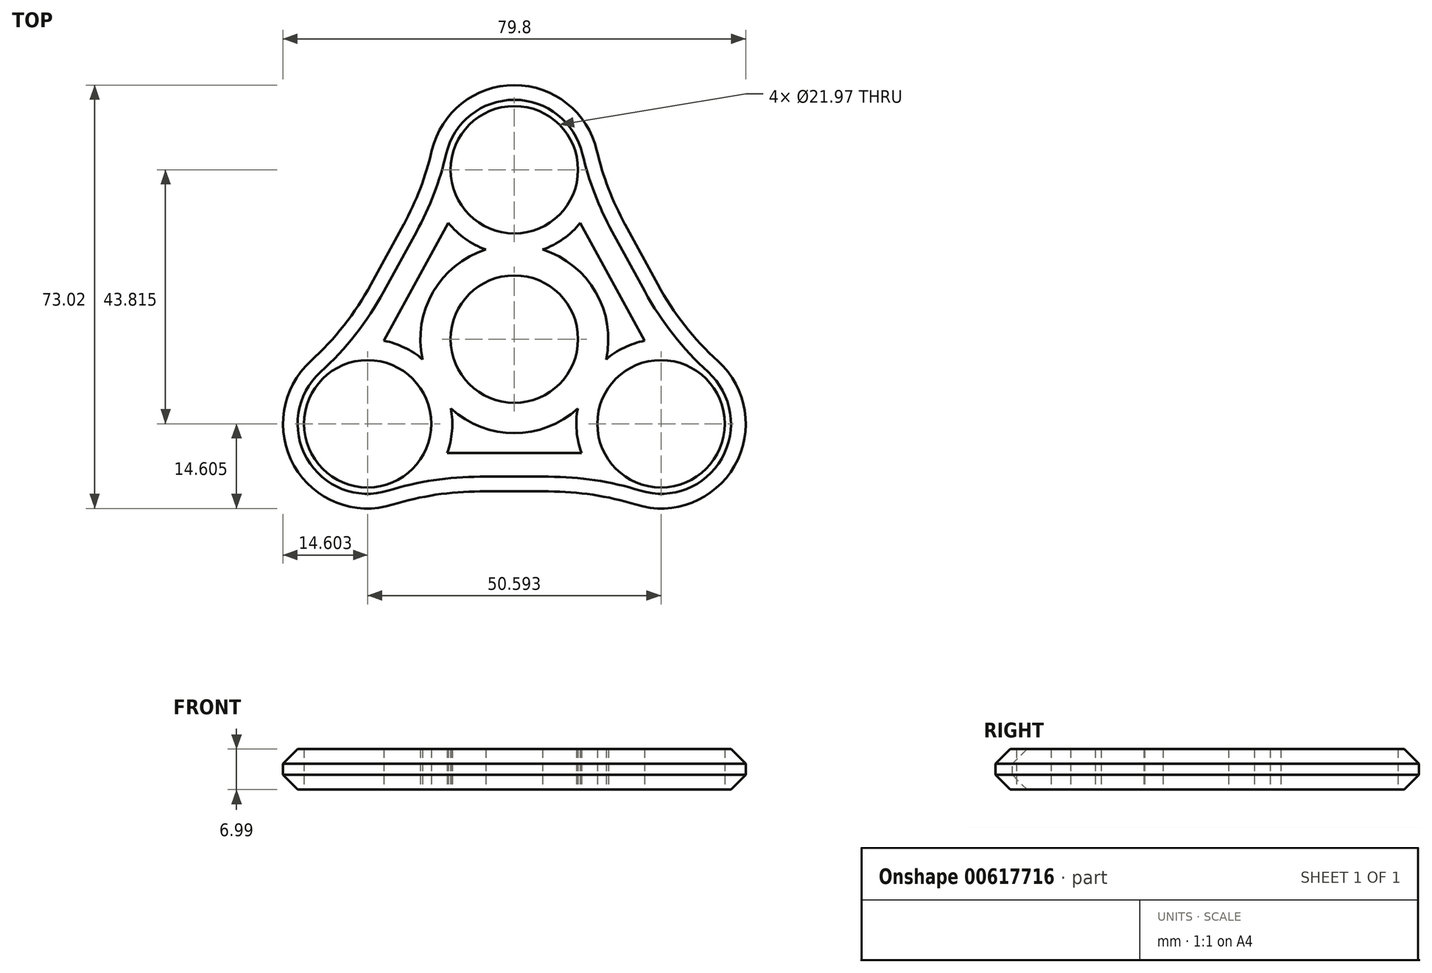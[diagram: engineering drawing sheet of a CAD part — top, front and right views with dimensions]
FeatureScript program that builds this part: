
annotation { "Feature Type Name" : "Feature", "Feature Type Description" : "" }
export const myFeature = defineFeature(function(context is Context, id is Id, definition is map)
    precondition{}
    {
        {
            var Q0;
            Q0=qCreatedBy(makeId("Top.planeOp"),FACE);
            var sketch = newSketch(context, id + "F0", { "sketchPlane" : qUnion([Q0])});
            skCircle(sketch, "E0", {"center": v(0, 0) * mm, "radius": 10.99 * mm});
            skLineSegment(sketch, "E1", {"start": v(0, 0) * mm, "end": v(0, 29.21) * mm});
            skLineSegment(sketch, "E2", {"start": v(0, 0) * mm, "end": v(25.3, -14.6) * mm});
            skLineSegment(sketch, "E3", {"start": v(0, 0) * mm, "end": v(-25.3, -14.6) * mm});
            skCircle(sketch, "E4", {"center": v(-25.3, -14.6) * mm, "radius": 10.99 * mm});
            skCircle(sketch, "E5", {"center": v(25.3, -14.6) * mm, "radius": 10.99 * mm});
            skCircle(sketch, "E6", {"center": v(0, 29.21) * mm, "radius": 10.99 * mm});
            skCircle(sketch, "E7", {"center": v(-25.3, -14.6) * mm, "radius": 14.6 * mm});
            skCircle(sketch, "E8", {"center": v(0, 29.21) * mm, "radius": 14.6 * mm});
            skCircle(sketch, "E9", {"center": v(25.3, -14.6) * mm, "radius": 14.6 * mm});
            skLineSegment(sketch, "E10", {"start": v(-16.5, -26.27) * mm, "end": v(16.51, -26.27) * mm});
            skLineSegment(sketch, "E11", {"start": v(11.38, 20.05) * mm, "end": v(22.47, -0.28) * mm});
            skLineSegment(sketch, "E12", {"start": v(-11.58, -19.62) * mm, "end": v(11.58, -19.62) * mm});
            skLineSegment(sketch, "E13", {"start": v(14.56, 28.07) * mm, "end": v(30.38, -0.91) * mm});
            skLineSegment(sketch, "E14", {"start": v(-14.56, 28.07) * mm, "end": v(-30.38, -0.91) * mm});
            skLineSegment(sketch, "E15", {"start": v(-11.38, 20.05) * mm, "end": v(-22.47, -0.28) * mm});
            skPoint(sketch, "E15.endSnap0", {"position": v(-22.47, 13.58) * mm});
            skCircle(sketch, "E16", {"center": v(0, 0) * mm, "radius": 16.2 * mm});
            skSolve(sketch);
        }
        {
            var Q0;
            {var subQ0=sQuery(id+"F0.wireOp",EDGE,"E14");Q0=makeQuery(id+"F0.imprint","IMPRINT",FACE,{"disambiguationData":[TD([[makeQuery(id+"F0.imprint","IMPRINT",EDGE,{"derivedFrom":subQ0}),1.0]])]});}
            var Q1;
            {var subQ0=sQuery(id+"F0.wireOp",EDGE,"E11");Q1=makeQuery(id+"F0.imprint","IMPRINT",FACE,{"disambiguationData":[TD([[makeQuery(id+"F0.imprint","IMPRINT",EDGE,{"derivedFrom":subQ0}),1.0]])]});}
            var Q2;
            Q2=makeQuery(id+"F0.imprint","IMPRINT",FACE,{"disambiguationData":[TD([[makeQuery(id+"F0.imprint","IMPRINT",EDGE,{"derivedFrom":sQuery(id+"F0.wireOp",EDGE,"E6")}),-1.0]])]});
            var Q3;
            {var subQ0=sQuery(id+"F0.wireOp",EDGE,"E16");var subQ1=sQuery(id+"F0.wireOp",EDGE,"E1");var subQ2=makeQuery(id+"F0.imprint","INTERSECT",VERTEX,{"derivedFrom":[subQ1,subQ0]});Q3=makeQuery(id+"F0.imprint","IMPRINT",FACE,{"disambiguationData":[TD([[makeQuery(id+"F0.imprint","IMPRINT",EDGE,{"disambiguationData":[TD([[subQ2,1.0]])],"derivedFrom":subQ1}),-1.0]])]});}
            var Q4;
            {var subQ0=sQuery(id+"F0.wireOp",EDGE,"E16");var subQ1=sQuery(id+"F0.wireOp",EDGE,"E1");var subQ2=makeQuery(id+"F0.imprint","INTERSECT",VERTEX,{"derivedFrom":[subQ1,subQ0]});Q4=makeQuery(id+"F0.imprint","IMPRINT",FACE,{"disambiguationData":[TD([[makeQuery(id+"F0.imprint","IMPRINT",EDGE,{"disambiguationData":[TD([[subQ2,1.0]])],"derivedFrom":subQ1}),1.0]])]});}
            var Q5;
            {var subQ1=sQuery(id+"F0.wireOp",EDGE,"E1");var subQ5=sQuery(id+"F0.wireOp",EDGE,"E0");var subQ6=makeQuery(id+"F0.imprint","INTERSECT",VERTEX,{"derivedFrom":[subQ5,subQ1]});Q5=makeQuery(id+"F0.imprint","IMPRINT",FACE,{"disambiguationData":[TD([[makeQuery(id+"F0.imprint","IMPRINT",EDGE,{"disambiguationData":[TD([[subQ6,1.0]])],"derivedFrom":subQ5}),-1.0]])]});}
            var Q6;
            {var subQ1=sQuery(id+"F0.wireOp",EDGE,"E3");var subQ6=sQuery(id+"F0.wireOp",EDGE,"E0");var subQ10=makeQuery(id+"F0.imprint","INTERSECT",VERTEX,{"derivedFrom":[subQ6,subQ1]});Q6=makeQuery(id+"F0.imprint","IMPRINT",FACE,{"disambiguationData":[TD([[makeQuery(id+"F0.imprint","IMPRINT",EDGE,{"disambiguationData":[TD([[subQ10,1.0]])],"derivedFrom":subQ6}),-1.0]])]});}
            var Q7;
            {var subQ1=sQuery(id+"F0.wireOp",EDGE,"E3");var subQ5=sQuery(id+"F0.wireOp",EDGE,"E0");var subQ6=makeQuery(id+"F0.imprint","INTERSECT",VERTEX,{"derivedFrom":[subQ5,subQ1]});Q7=makeQuery(id+"F0.imprint","IMPRINT",FACE,{"disambiguationData":[TD([[makeQuery(id+"F0.imprint","IMPRINT",EDGE,{"disambiguationData":[TD([[subQ6,-1.0]])],"derivedFrom":subQ5}),-1.0]])]});}
            var Q8;
            {var subQ0=sQuery(id+"F0.wireOp",EDGE,"E10");Q8=makeQuery(id+"F0.imprint","IMPRINT",FACE,{"disambiguationData":[TD([[makeQuery(id+"F0.imprint","IMPRINT",EDGE,{"derivedFrom":subQ0}),1.0]])]});}
            var Q9;
            Q9=makeQuery(id+"F0.imprint","IMPRINT",FACE,{"disambiguationData":[TD([[makeQuery(id+"F0.imprint","IMPRINT",EDGE,{"derivedFrom":sQuery(id+"F0.wireOp",EDGE,"E4")}),-1.0]])]});
            var Q10;
            {var subQ0=sQuery(id+"F0.wireOp",EDGE,"E16");var subQ1=sQuery(id+"F0.wireOp",EDGE,"E3");var subQ2=makeQuery(id+"F0.imprint","INTERSECT",VERTEX,{"derivedFrom":[subQ1,subQ0]});Q10=makeQuery(id+"F0.imprint","IMPRINT",FACE,{"disambiguationData":[TD([[makeQuery(id+"F0.imprint","IMPRINT",EDGE,{"disambiguationData":[TD([[subQ2,1.0]])],"derivedFrom":subQ1}),1.0]])]});}
            var Q11;
            {var subQ0=sQuery(id+"F0.wireOp",EDGE,"E16");var subQ1=sQuery(id+"F0.wireOp",EDGE,"E3");var subQ2=makeQuery(id+"F0.imprint","INTERSECT",VERTEX,{"derivedFrom":[subQ1,subQ0]});Q11=makeQuery(id+"F0.imprint","IMPRINT",FACE,{"disambiguationData":[TD([[makeQuery(id+"F0.imprint","IMPRINT",EDGE,{"disambiguationData":[TD([[subQ2,1.0]])],"derivedFrom":subQ1}),-1.0]])]});}
            var Q12;
            {var subQ0=sQuery(id+"F0.wireOp",EDGE,"E16");var subQ1=sQuery(id+"F0.wireOp",EDGE,"E2");var subQ2=makeQuery(id+"F0.imprint","INTERSECT",VERTEX,{"derivedFrom":[subQ1,subQ0]});Q12=makeQuery(id+"F0.imprint","IMPRINT",FACE,{"disambiguationData":[TD([[makeQuery(id+"F0.imprint","IMPRINT",EDGE,{"disambiguationData":[TD([[subQ2,1.0]])],"derivedFrom":subQ1}),-1.0]])]});}
            var Q13;
            Q13=makeQuery(id+"F0.imprint","IMPRINT",FACE,{"disambiguationData":[TD([[makeQuery(id+"F0.imprint","IMPRINT",EDGE,{"derivedFrom":sQuery(id+"F0.wireOp",EDGE,"E5")}),-1.0]])]});
            var Q14;
            {var subQ0=sQuery(id+"F0.wireOp",EDGE,"E16");var subQ1=sQuery(id+"F0.wireOp",EDGE,"E2");var subQ2=makeQuery(id+"F0.imprint","INTERSECT",VERTEX,{"derivedFrom":[subQ1,subQ0]});Q14=makeQuery(id+"F0.imprint","IMPRINT",FACE,{"disambiguationData":[TD([[makeQuery(id+"F0.imprint","IMPRINT",EDGE,{"disambiguationData":[TD([[subQ2,1.0]])],"derivedFrom":subQ1}),1.0]])]});}
            extrude(context, id + "F1", {"entities" : qUnion([Q0, Q1, Q2, Q3, Q4, Q5, Q6, Q7, Q8, Q9, Q10, Q11, Q12, Q13, Q14]), "depth" : 7 * mm, "offsetDistance" : 25.4 * mm});
        }
        {
            var Q0;
            Q0=makeQuery(id+"F1.opExtrude","SWEPT_EDGE",EDGE,{"disambiguationData":[OSD([sQuery(id+"F0.wireOp",EDGE,"E8"),sQuery(id+"F0.wireOp",EDGE,"E14")])]});
            var Q1;
            Q1=makeQuery(id+"F1.opExtrude","SWEPT_EDGE",EDGE,{"disambiguationData":[OSD([sQuery(id+"F0.wireOp",EDGE,"E7"),sQuery(id+"F0.wireOp",EDGE,"E14")])]});
            var Q2;
            Q2=makeQuery(id+"F1.opExtrude","SWEPT_EDGE",EDGE,{"disambiguationData":[OSD([sQuery(id+"F0.wireOp",EDGE,"E9"),sQuery(id+"F0.wireOp",EDGE,"E10")])]});
            var Q3;
            Q3=makeQuery(id+"F1.opExtrude","SWEPT_EDGE",EDGE,{"disambiguationData":[OSD([sQuery(id+"F0.wireOp",EDGE,"E7"),sQuery(id+"F0.wireOp",EDGE,"E10")])]});
            var Q4;
            Q4=makeQuery(id+"F1.opExtrude","SWEPT_EDGE",EDGE,{"disambiguationData":[OSD([sQuery(id+"F0.wireOp",EDGE,"E8"),sQuery(id+"F0.wireOp",EDGE,"E13")])]});
            var Q5;
            Q5=makeQuery(id+"F1.opExtrude","SWEPT_EDGE",EDGE,{"disambiguationData":[OSD([sQuery(id+"F0.wireOp",EDGE,"E9"),sQuery(id+"F0.wireOp",EDGE,"E13")])]});
            fillet(context, id + "F2", {"entities" : qUnion([Q0, Q1, Q2, Q3, Q4, Q5]), "radius" : 50.8 * mm, "tangentPropagation" : true, "allowEdgeOverflow" : false});
        }
        {
            var Q0;
            {var subQ0=sQuery(id+"F0.wireOp",EDGE,"E7");Q0=makeQuery(id+"F1.opExtrude","CAP_EDGE",EDGE,{"disambiguationData":[OSD([subQ0]),TDD([makeQuery(id+"F0.imprint","IMPRINT",EDGE,{"disambiguationData":[TD([[makeQuery(id+"F0.imprint","INTERSECT",VERTEX,{"derivedFrom":[subQ0,sQuery(id+"F0.wireOp",EDGE,"E10")]}),1.0]])],"derivedFrom":subQ0})])],"isStart":true});}
            var Q1;
            {var subQ0=sQuery(id+"F0.wireOp",EDGE,"E7");Q1=makeQuery(id+"F1.opExtrude","CAP_EDGE",EDGE,{"disambiguationData":[OSD([subQ0]),TDD([makeQuery(id+"F0.imprint","IMPRINT",EDGE,{"disambiguationData":[TD([[makeQuery(id+"F0.imprint","INTERSECT",VERTEX,{"derivedFrom":[subQ0,sQuery(id+"F0.wireOp",EDGE,"E10")]}),1.0]])],"derivedFrom":subQ0})])],"isStart":false});}
            chamfer(context, id + "F3", {"entities" : qUnion([Q0, Q1]), "width" : 2.54 * mm, "tangentPropagation" : true});
        }
    });
